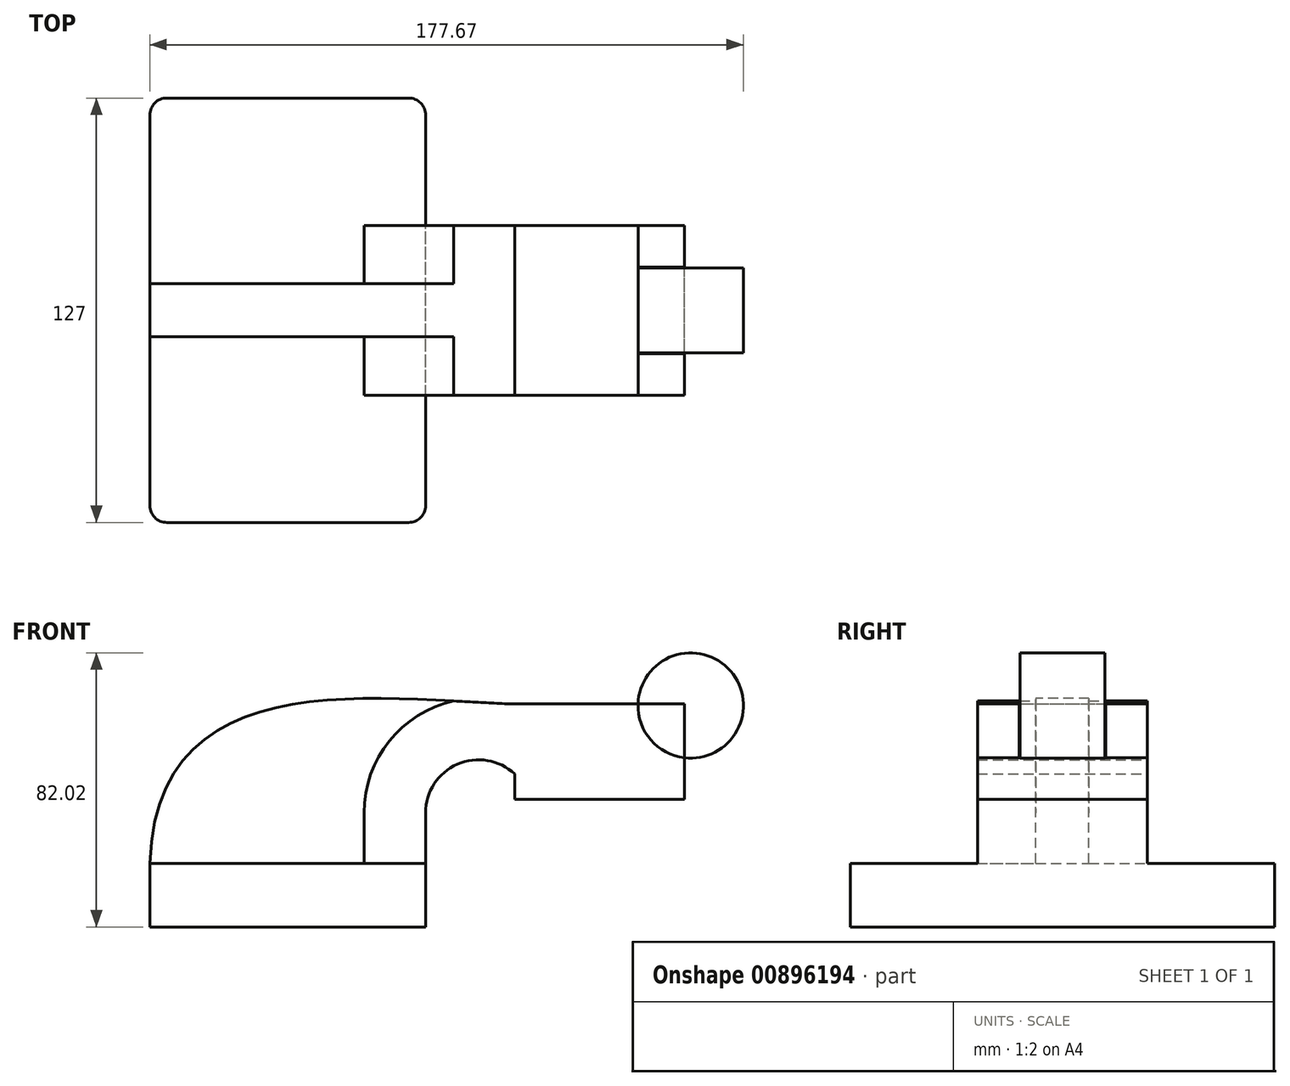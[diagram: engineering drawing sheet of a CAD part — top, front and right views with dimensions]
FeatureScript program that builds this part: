
annotation { "Feature Type Name" : "Feature", "Feature Type Description" : "" }
export const myFeature = defineFeature(function(context is Context, id is Id, definition is map)
    precondition{}
    {
        {
            var Q0;
            Q0=qCreatedBy(makeId("Front.planeOp"),FACE);
            var sketch = newSketch(context, id + "F0", { "sketchPlane" : qUnion([Q0])});
            skLineSegment(sketch, "E0.bottom", {"start": v(41.27, 9.53) * mm, "end": v(-41.28, 9.53) * mm});
            skLineSegment(sketch, "E0.top", {"start": v(41.28, -9.52) * mm, "end": v(-41.27, -9.52) * mm});
            skLineSegment(sketch, "E0.left", {"start": v(41.28, 9.53) * mm, "end": v(41.28, -9.52) * mm});
            skLineSegment(sketch, "E0.right", {"start": v(-41.28, 9.53) * mm, "end": v(-41.27, -9.52) * mm});
            skPoint(sketch, "E0.middle", {"position": v(0, 0) * mm});
            skLineSegment(sketch, "E1.bottom", {"start": v(118.73, 28.59) * mm, "end": v(67.93, 28.59) * mm});
            skLineSegment(sketch, "E1.top", {"start": v(118.73, 57.16) * mm, "end": v(67.93, 57.16) * mm});
            skLineSegment(sketch, "E1.left", {"start": v(118.73, 28.59) * mm, "end": v(118.73, 57.16) * mm});
            skLineSegment(sketch, "E1.right", {"start": v(67.93, 28.59) * mm, "end": v(67.93, 57.16) * mm});
            skPoint(sketch, "E1.middle", {"position": v(93.33, 42.88) * mm});
            skLineSegment(sketch, "E2", {"start": v(41.27, 9.53) * mm, "end": v(41.27, 24.6) * mm});
            skArc(sketch, "E3", {"start": v(41.28, 24.6) * mm, "mid": v(51.32, 39.37) * mm, "end": v(68.74, 35.46) * mm});
            skLineSegment(sketch, "E4", {"start": v(93.33, 42.88) * mm, "end": v(68.74, 42.88) * mm});
            skLineSegment(sketch, "E5.0", {"start": v(41.28, -40.26) * mm, "end": v(-41.27, -40.26) * mm});
            skArc(sketch, "E6.0", {"start": v(22.86, 24.6) * mm, "mid": v(37.07, 52.4) * mm, "end": v(67.93, 57.16) * mm});
            skLineSegment(sketch, "E6.1", {"start": v(22.86, 9.53) * mm, "end": v(22.86, 24.6) * mm});
            skFitSpline(sketch, "E7", {"points": [v(-41.28, 9.52) * mm, v(67.93, 57.16) * mm], "startDerivative": vector(5.65, 179.52) * mm, "endDerivative": vector(129.44, -4.72) * mm});
            skLineSegment(sketch, "E8", {"start": v(67.93, 57.16) * mm, "end": v(67.93, 57.16) * mm});
            skLineSegment(sketch, "E9", {"start": v(118.73, 57.16) * mm, "end": v(118.73, 28.59) * mm});
            skCircle(sketch, "E10", {"center": v(120.63, 56.72) * mm, "radius": 15.76 * mm});
            skSolve(sketch);
        }
        {
            var Q0;
            Q0=makeQuery(id+"F0.imprint","IMPRINT",FACE,{"disambiguationData":[TD([[makeQuery(id+"F0.imprint","IMPRINT",EDGE,{"derivedFrom":sQuery(id+"F0.wireOp",EDGE,"E0.top")}),-1.0]])]});
            extrude(context, id + "F1", {"entities" : qUnion([Q0]), "endBound" : BoundingType.SYMMETRIC, "depth" : 127 * mm, "offsetDistance" : 25.4 * mm});
        }
        {
            var Q0;
            {var subQ0=sQuery(id+"F0.wireOp",EDGE,"E8");Q0=makeQuery(id+"F0.imprint","IMPRINT",FACE,{"disambiguationData":[TD([[makeQuery(id+"F0.imprint","IMPRINT",EDGE,{"derivedFrom":subQ0}),-1.0]])]});}
            var Q1;
            {var subQ1=sQuery(id+"F0.wireOp",EDGE,"E2");Q1=makeQuery(id+"F0.imprint","IMPRINT",FACE,{"disambiguationData":[TD([[makeQuery(id+"F0.imprint","IMPRINT",EDGE,{"derivedFrom":subQ1}),1.0]])]});}
            var Q2;
            {var subQ1=sQuery(id+"F0.wireOp",EDGE,"E1.bottom");Q2=makeQuery(id+"F0.imprint","IMPRINT",FACE,{"disambiguationData":[TD([[makeQuery(id+"F0.imprint","IMPRINT",EDGE,{"derivedFrom":subQ1}),-1.0]])]});}
            extrude(context, id + "F2", {"entities" : qUnion([Q0, Q1, Q2]), "operationType" : NewBodyOperationType.ADD, "endBound" : BoundingType.SYMMETRIC, "depth" : 50.8 * mm, "offsetDistance" : 25.4 * mm});
        }
        {
            var Q0;
            {var subQ3=sQuery(id+"F0.wireOp",EDGE,"E6.1");Q0=makeQuery(id+"F0.imprint","IMPRINT",FACE,{"disambiguationData":[TD([[makeQuery(id+"F0.imprint","IMPRINT",EDGE,{"derivedFrom":subQ3}),1.0]])]});}
            extrude(context, id + "F3", {"entities" : qUnion([Q0]), "operationType" : NewBodyOperationType.ADD, "endBound" : BoundingType.SYMMETRIC, "depth" : 15.88 * mm, "offsetDistance" : 25.4 * mm});
        }
        {
            var Q0;
            Q0=makeQuery(id+"F1.opExtrude","CAP_EDGE",EDGE,{"disambiguationData":[OSD([sQuery(id+"F0.wireOp",EDGE,"E0.right")])],"isStart":false});
            var Q1;
            Q1=makeQuery(id+"F1.opExtrude","CAP_EDGE",EDGE,{"disambiguationData":[OSD([sQuery(id+"F0.wireOp",EDGE,"E0.left")])],"isStart":false});
            var Q2;
            Q2=makeQuery(id+"F1.opExtrude","CAP_EDGE",EDGE,{"disambiguationData":[OSD([sQuery(id+"F0.wireOp",EDGE,"E0.left")])],"isStart":true});
            var Q3;
            Q3=makeQuery(id+"F1.opExtrude","CAP_EDGE",EDGE,{"disambiguationData":[OSD([sQuery(id+"F0.wireOp",EDGE,"E0.right")])],"isStart":true});
            fillet(context, id + "F4", {"entities" : qUnion([Q0, Q1, Q2, Q3]), "radius" : 5.08 * mm, "tangentPropagation" : true, "allowEdgeOverflow" : false});
        }
        {
            var Q0;
            {var subQ0=sQuery(id+"F0.wireOp",EDGE,"E9");var subQ1=sQuery(id+"F0.wireOp",EDGE,"E1.top");var subQ2=makeQuery(id+"F0.imprint","INTERSECT",VERTEX,{"derivedFrom":[subQ1,subQ0]});Q0=makeQuery(id+"F0.imprint","IMPRINT",FACE,{"disambiguationData":[TD([[makeQuery(id+"F0.imprint","IMPRINT",EDGE,{"disambiguationData":[TD([[subQ2,-1.0]])],"derivedFrom":subQ1}),-1.0]])]});}
            extrude(context, id + "F5", {"entities" : qUnion([Q0]), "endBound" : BoundingType.SYMMETRIC, "depth" : 25.4 * mm, "offsetDistance" : 25.4 * mm});
        }
        {
            var Q0;
            {var subQ0=sQuery(id+"F0.wireOp",EDGE,"E9");var subQ1=sQuery(id+"F0.wireOp",EDGE,"E1.top");var subQ2=makeQuery(id+"F0.imprint","INTERSECT",VERTEX,{"derivedFrom":[subQ1,subQ0]});Q0=makeQuery(id+"F0.imprint","IMPRINT",FACE,{"disambiguationData":[TD([[makeQuery(id+"F0.imprint","IMPRINT",EDGE,{"disambiguationData":[TD([[subQ2,-1.0]])],"derivedFrom":subQ1}),1.0]])]});}
            extrude(context, id + "F6", {"entities" : qUnion([Q0]), "endBound" : BoundingType.SYMMETRIC, "depth" : 25.9 * mm, "offsetDistance" : 25.4 * mm});
        }
    });
